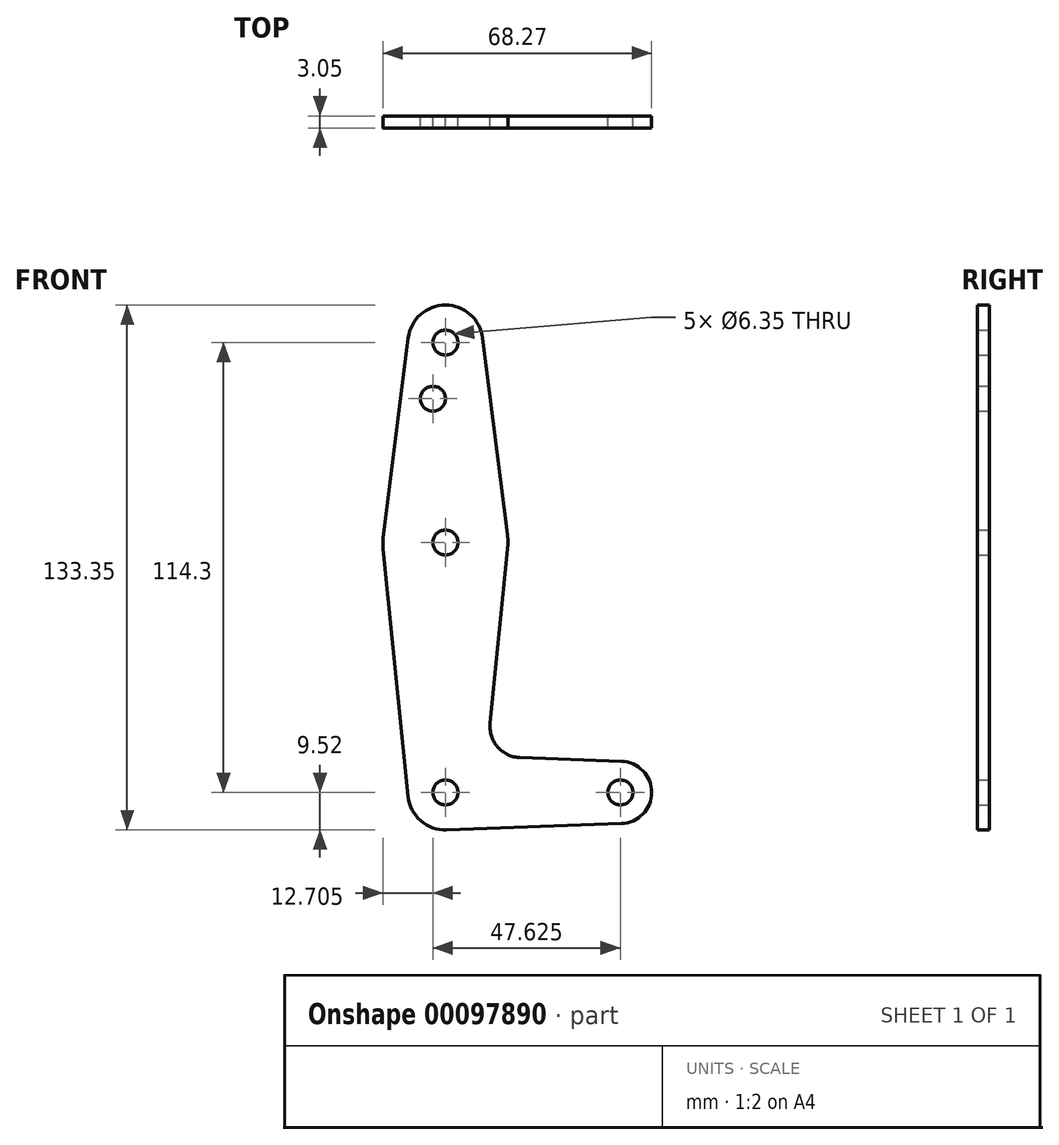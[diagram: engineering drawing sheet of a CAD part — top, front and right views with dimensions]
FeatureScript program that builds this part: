
annotation { "Feature Type Name" : "Feature", "Feature Type Description" : "" }
export const myFeature = defineFeature(function(context is Context, id is Id, definition is map)
    precondition{}
    {
        {
            var Q0;
            Q0=qCreatedBy(makeId("Front.planeOp"),FACE);
            var sketch = newSketch(context, id + "F0", { "sketchPlane" : qUnion([Q0])});
            skLineSegment(sketch, "E0", {"start": v(0, 114.3) * mm, "end": v(0, 0) * mm, "construction": true});
            skLineSegment(sketch, "E1", {"start": v(0, 0) * mm, "end": v(44.45, 0) * mm, "construction": true});
            skCircle(sketch, "E2", {"center": v(0, 114.3) * mm, "radius": 9.53 * mm});
            skCircle(sketch, "E3", {"center": v(0, 63.5) * mm, "radius": 15.88 * mm});
            skCircle(sketch, "E4", {"center": v(0, 0) * mm, "radius": 9.53 * mm});
            skCircle(sketch, "E5", {"center": v(44.45, 0) * mm, "radius": 7.94 * mm});
            skLineSegment(sketch, "E6", {"start": v(9.45, 115.5) * mm, "end": v(15.75, 65.48) * mm});
            skLineSegment(sketch, "E7", {"start": v(-9.45, 115.5) * mm, "end": v(-15.75, 65.48) * mm});
            skLineSegment(sketch, "E8", {"start": v(-15.8, 61.91) * mm, "end": v(-9.48, -0.95) * mm});
            skLineSegment(sketch, "E9", {"start": v(15.8, 61.91) * mm, "end": v(11.34, 17.6) * mm});
            skLineSegment(sketch, "E10", {"start": v(18.97, 8.85) * mm, "end": v(44.73, 7.93) * mm});
            skLineSegment(sketch, "E11", {"start": v(0.34, -9.52) * mm, "end": v(44.73, -7.93) * mm});
            skCircle(sketch, "E12", {"center": v(0, 114.3) * mm, "radius": 3.18 * mm});
            skCircle(sketch, "E13", {"center": v(-3.17, 100.03) * mm, "radius": 3.18 * mm});
            skCircle(sketch, "E14", {"center": v(0, 63.5) * mm, "radius": 3.18 * mm});
            skCircle(sketch, "E15", {"center": v(0, 0) * mm, "radius": 3.18 * mm});
            skCircle(sketch, "E16", {"center": v(44.45, 0) * mm, "radius": 3.18 * mm});
            skArc(sketch, "E17.filletArc", {"start": v(11.34, 17.6) * mm, "mid": v(13.26, 11.57) * mm, "end": v(18.97, 8.85) * mm});
            skSolve(sketch);
        }
        {
            var Q0;
            Q0=makeQuery(id+"F0.imprint","IMPRINT",FACE,{"disambiguationData":[TD([[makeQuery(id+"F0.imprint","IMPRINT",EDGE,{"derivedFrom":sQuery(id+"F0.wireOp",EDGE,"E12")}),-1.0]])]});
            var Q1;
            {var subQ1=sQuery(id+"F0.wireOp",EDGE,"E6");Q1=makeQuery(id+"F0.imprint","IMPRINT",FACE,{"disambiguationData":[TD([[makeQuery(id+"F0.imprint","IMPRINT",EDGE,{"derivedFrom":subQ1}),-1.0]])]});}
            var Q2;
            Q2=makeQuery(id+"F0.imprint","IMPRINT",FACE,{"disambiguationData":[TD([[makeQuery(id+"F0.imprint","IMPRINT",EDGE,{"derivedFrom":sQuery(id+"F0.wireOp",EDGE,"E14")}),-1.0]])]});
            var Q3;
            {var subQ0=sQuery(id+"F0.wireOp",EDGE,"E8");Q3=makeQuery(id+"F0.imprint","IMPRINT",FACE,{"disambiguationData":[TD([[makeQuery(id+"F0.imprint","IMPRINT",EDGE,{"derivedFrom":subQ0}),1.0]])]});}
            var Q4;
            Q4=makeQuery(id+"F0.imprint","IMPRINT",FACE,{"disambiguationData":[TD([[makeQuery(id+"F0.imprint","IMPRINT",EDGE,{"derivedFrom":sQuery(id+"F0.wireOp",EDGE,"E15")}),-1.0]])]});
            var Q5;
            Q5=makeQuery(id+"F0.imprint","IMPRINT",FACE,{"disambiguationData":[TD([[makeQuery(id+"F0.imprint","IMPRINT",EDGE,{"derivedFrom":sQuery(id+"F0.wireOp",EDGE,"E16")}),-1.0]])]});
            extrude(context, id + "F1", {"entities" : qUnion([Q0, Q1, Q2, Q3, Q4, Q5]), "depth" : 3.05 * mm});
        }
    });
